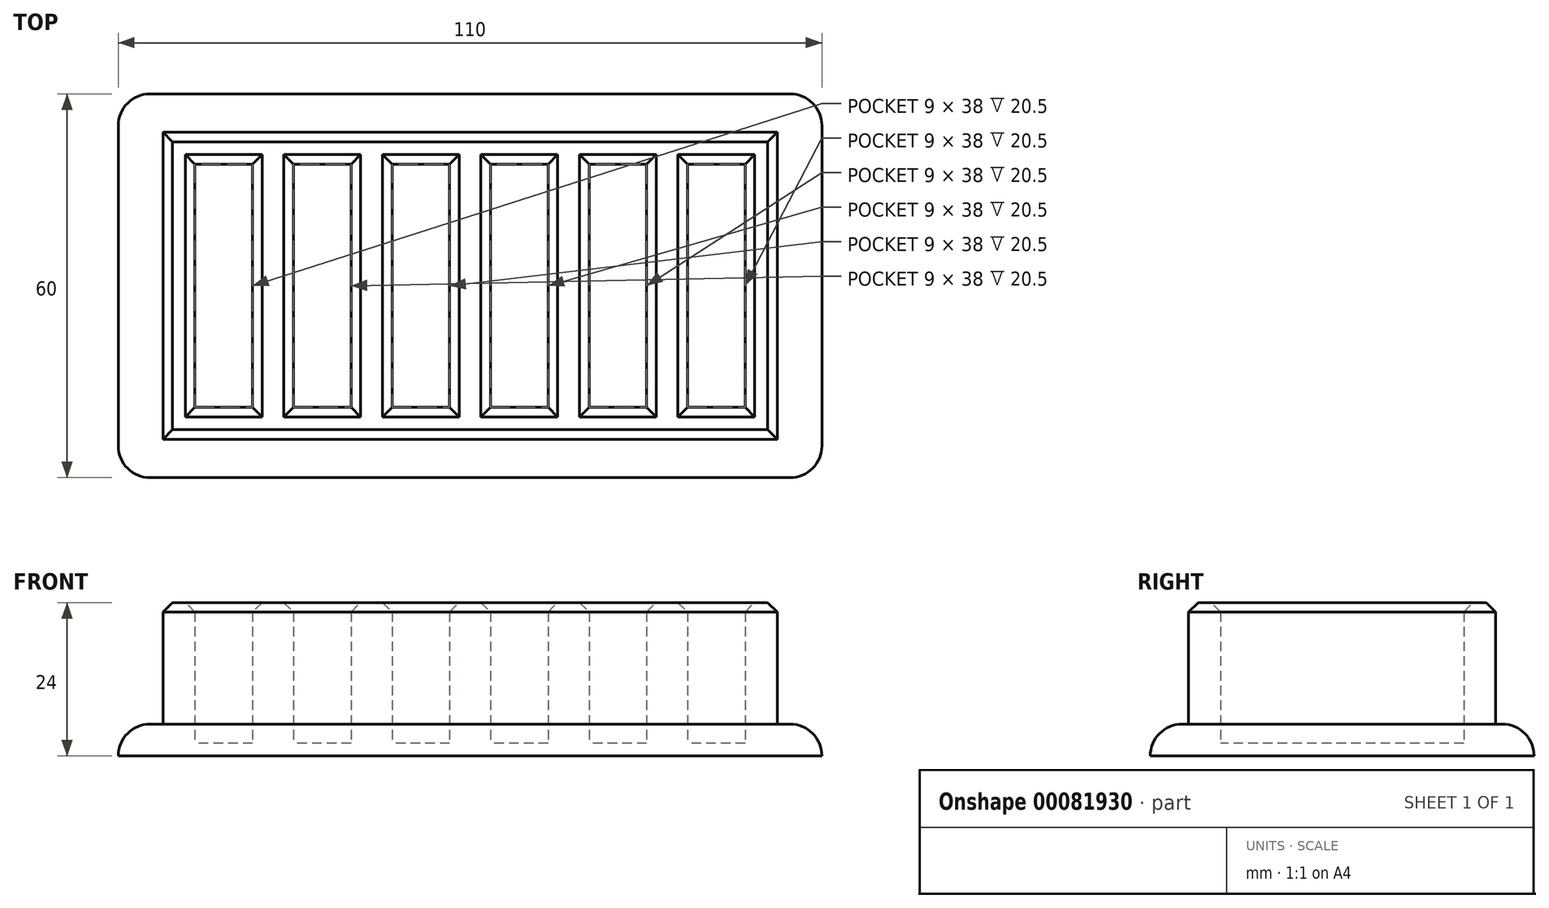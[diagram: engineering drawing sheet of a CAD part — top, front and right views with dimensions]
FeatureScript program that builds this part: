
annotation { "Feature Type Name" : "Feature", "Feature Type Description" : "" }
export const myFeature = defineFeature(function(context is Context, id is Id, definition is map)
    precondition{}
    {
        {
            var Q0;
            Q0=qCreatedBy(makeId("Top.planeOp"),FACE);
            var sketch = newSketch(context, id + "F0", { "sketchPlane" : qUnion([Q0])});
            skLineSegment(sketch, "E0.rect.bottom", {"start": v(48, 24) * mm, "end": v(-48, 24) * mm});
            skLineSegment(sketch, "E0.rect.top", {"start": v(48, -24) * mm, "end": v(-48, -24) * mm});
            skLineSegment(sketch, "E0.rect.left", {"start": v(48, 24) * mm, "end": v(48, -24) * mm});
            skLineSegment(sketch, "E0.rect.right", {"start": v(-48, 24) * mm, "end": v(-48, -24) * mm});
            skPoint(sketch, "E0.rect.middle", {"position": v(0, 0) * mm});
            skLineSegment(sketch, "E1.rect.bottom", {"start": v(-55, 30) * mm, "end": v(55, 30) * mm});
            skLineSegment(sketch, "E1.rect.top", {"start": v(-55, -30) * mm, "end": v(55, -30) * mm});
            skLineSegment(sketch, "E1.rect.left", {"start": v(-55, 30) * mm, "end": v(-55, -30) * mm});
            skLineSegment(sketch, "E1.rect.right", {"start": v(55, 30) * mm, "end": v(55, -30) * mm});
            skSolve(sketch);
        }
        {
            var Q0;
            Q0=makeQuery(id+"F0.imprint","IMPRINT",FACE,{"disambiguationData":[TD([[makeQuery(id+"F0.imprint","IMPRINT",EDGE,{"derivedFrom":sQuery(id+"F0.wireOp",EDGE,"E0.rect.bottom")}),1.0]])]});
            extrude(context, id + "F1", {"entities" : qUnion([Q0]), "depth" : 2 * mm});
        }
        {
            var Q0;
            Q0=makeQuery(id+"F1.opExtrude","CAP_FACE",FACE,{"disambiguationData":[OSD([sQuery(id+"F0.wireOp",EDGE,"E0.rect.bottom"),sQuery(id+"F0.wireOp",EDGE,"E0.rect.top"),sQuery(id+"F0.wireOp",EDGE,"E0.rect.left"),sQuery(id+"F0.wireOp",EDGE,"E0.rect.right")])],"isStart":false});
            var sketch = newSketch(context, id + "F2", { "sketchPlane" : qUnion([Q0])});
            skLineSegment(sketch, "E2.rect.bottom", {"start": v(-34, 19) * mm, "end": v(-43, 19) * mm});
            skLineSegment(sketch, "E2.rect.top", {"start": v(-34, -19) * mm, "end": v(-43, -19) * mm});
            skLineSegment(sketch, "E2.rect.left", {"start": v(-34, 19) * mm, "end": v(-34, -19) * mm});
            skLineSegment(sketch, "E2.rect.right", {"start": v(-43, 19) * mm, "end": v(-43, -19) * mm});
            skPoint(sketch, "E2.rect.middle", {"position": v(-38.5, 0) * mm});
            skLineSegment(sketch, "E3.1.0.0", {"start": v(-18.6, 19) * mm, "end": v(-18.6, -19) * mm});
            skLineSegment(sketch, "E3.1.0.1", {"start": v(-27.6, 19) * mm, "end": v(-27.6, -19) * mm});
            skLineSegment(sketch, "E3.1.0.2", {"start": v(-18.6, 19) * mm, "end": v(-27.6, 19) * mm});
            skLineSegment(sketch, "E3.1.0.3", {"start": v(-18.6, -19) * mm, "end": v(-27.6, -19) * mm});
            skLineSegment(sketch, "E3.2.0.0", {"start": v(-3.2, 19) * mm, "end": v(-3.2, -19) * mm});
            skLineSegment(sketch, "E3.2.0.1", {"start": v(-12.2, 19) * mm, "end": v(-12.2, -19) * mm});
            skLineSegment(sketch, "E3.2.0.2", {"start": v(-3.2, 19) * mm, "end": v(-12.2, 19) * mm});
            skLineSegment(sketch, "E3.2.0.3", {"start": v(-3.2, -19) * mm, "end": v(-12.2, -19) * mm});
            skLineSegment(sketch, "E3.3.0.0", {"start": v(12.2, 19) * mm, "end": v(12.2, -19) * mm});
            skLineSegment(sketch, "E3.3.0.1", {"start": v(3.2, 19) * mm, "end": v(3.2, -19) * mm});
            skLineSegment(sketch, "E3.3.0.2", {"start": v(12.2, 19) * mm, "end": v(3.2, 19) * mm});
            skLineSegment(sketch, "E3.3.0.3", {"start": v(12.2, -19) * mm, "end": v(3.2, -19) * mm});
            skLineSegment(sketch, "E3.4.0.0", {"start": v(27.6, 19) * mm, "end": v(27.6, -19) * mm});
            skLineSegment(sketch, "E3.4.0.1", {"start": v(18.6, 19) * mm, "end": v(18.6, -19) * mm});
            skLineSegment(sketch, "E3.4.0.2", {"start": v(27.6, 19) * mm, "end": v(18.6, 19) * mm});
            skLineSegment(sketch, "E3.4.0.3", {"start": v(27.6, -19) * mm, "end": v(18.6, -19) * mm});
            skLineSegment(sketch, "E3.5.0.0", {"start": v(43, 19) * mm, "end": v(43, -19) * mm});
            skLineSegment(sketch, "E3.5.0.1", {"start": v(34, 19) * mm, "end": v(34, -19) * mm});
            skLineSegment(sketch, "E3.5.0.2", {"start": v(43, 19) * mm, "end": v(34, 19) * mm});
            skLineSegment(sketch, "E3.5.0.3", {"start": v(43, -19) * mm, "end": v(34, -19) * mm});
            skLineSegment(sketch, "E3.direction1", {"start": v(-43, -19) * mm, "end": v(-27.6, -19) * mm, "construction": true});
            skSolve(sketch);
        }
        {
            var Q0;
            Q0=makeQuery(id+"F2.imprint","IMPRINT",FACE,{"disambiguationData":[TD([[makeQuery(id+"F2.imprint","IMPRINT",EDGE,{"derivedFrom":sQuery(id+"F2.wireOp",EDGE,"E2.rect.bottom")}),-1.0]])]});
            extrude(context, id + "F3", {"entities" : qUnion([Q0]), "operationType" : NewBodyOperationType.ADD, "depth" : 22 * mm});
        }
        {
            var Q0;
            Q0=makeQuery(id+"F0.imprint","IMPRINT",FACE,{"disambiguationData":[TD([[makeQuery(id+"F0.imprint","IMPRINT",EDGE,{"derivedFrom":sQuery(id+"F0.wireOp",EDGE,"E0.rect.bottom")}),-1.0]])]});
            extrude(context, id + "F4", {"entities" : qUnion([Q0]), "operationType" : NewBodyOperationType.ADD, "depth" : 5 * mm});
        }
        {
            var Q0;
            Q0=makeQuery(id+"F4.opExtrude","CAP_EDGE",EDGE,{"disambiguationData":[OSD([sQuery(id+"F0.wireOp",EDGE,"E1.rect.top")])],"isStart":false});
            var Q1;
            Q1=makeQuery(id+"F4.opExtrude","CAP_EDGE",EDGE,{"disambiguationData":[OSD([sQuery(id+"F0.wireOp",EDGE,"E1.rect.left")])],"isStart":false});
            var Q2;
            Q2=makeQuery(id+"F4.opExtrude","CAP_EDGE",EDGE,{"disambiguationData":[OSD([sQuery(id+"F0.wireOp",EDGE,"E1.rect.bottom")])],"isStart":false});
            var Q3;
            Q3=makeQuery(id+"F4.opExtrude","CAP_EDGE",EDGE,{"disambiguationData":[OSD([sQuery(id+"F0.wireOp",EDGE,"E1.rect.right")])],"isStart":false});
            var Q4;
            Q4=makeQuery(id+"F4.opExtrude","SWEPT_EDGE",EDGE,{"disambiguationData":[OSD([sQuery(id+"F0.wireOp",EDGE,"E1.rect.top"),sQuery(id+"F0.wireOp",EDGE,"E1.rect.right")])]});
            var Q5;
            Q5=makeQuery(id+"F4.opExtrude","SWEPT_EDGE",EDGE,{"disambiguationData":[OSD([sQuery(id+"F0.wireOp",EDGE,"E1.rect.bottom"),sQuery(id+"F0.wireOp",EDGE,"E1.rect.right")])]});
            var Q6;
            Q6=makeQuery(id+"F4.opExtrude","SWEPT_EDGE",EDGE,{"disambiguationData":[OSD([sQuery(id+"F0.wireOp",EDGE,"E1.rect.top"),sQuery(id+"F0.wireOp",EDGE,"E1.rect.left")])]});
            var Q7;
            Q7=makeQuery(id+"F4.opExtrude","SWEPT_EDGE",EDGE,{"disambiguationData":[OSD([sQuery(id+"F0.wireOp",EDGE,"E1.rect.bottom"),sQuery(id+"F0.wireOp",EDGE,"E1.rect.left")])]});
            fillet(context, id + "F5", {"entities" : qUnion([Q0, Q1, Q2, Q3, Q4, Q5, Q6, Q7]), "radius" : 5 * mm, "tangentPropagation" : true, "allowEdgeOverflow" : false});
        }
        {
            var Q0;
            Q0=makeQuery(id+"F3.opExtrude","CAP_EDGE",EDGE,{"disambiguationData":[OSD([sQuery(id+"F0.wireOp",EDGE,"E0.rect.top")])],"isStart":false});
            var Q1;
            Q1=makeQuery(id+"F3.opExtrude","CAP_EDGE",EDGE,{"disambiguationData":[OSD([sQuery(id+"F0.wireOp",EDGE,"E0.rect.right")])],"isStart":false});
            var Q2;
            Q2=makeQuery(id+"F3.opExtrude","CAP_EDGE",EDGE,{"disambiguationData":[OSD([sQuery(id+"F0.wireOp",EDGE,"E0.rect.bottom")])],"isStart":false});
            var Q3;
            Q3=makeQuery(id+"F3.opExtrude","CAP_EDGE",EDGE,{"disambiguationData":[OSD([sQuery(id+"F0.wireOp",EDGE,"E0.rect.left")])],"isStart":false});
            var Q4;
            Q4=makeQuery(id+"F3.opExtrude","CAP_EDGE",EDGE,{"disambiguationData":[OSD([sQuery(id+"F2.wireOp",EDGE,"E2.rect.right")])],"isStart":false});
            var Q5;
            Q5=makeQuery(id+"F3.opExtrude","CAP_EDGE",EDGE,{"disambiguationData":[OSD([sQuery(id+"F2.wireOp",EDGE,"E2.rect.left")])],"isStart":false});
            var Q6;
            Q6=makeQuery(id+"F3.opExtrude","CAP_EDGE",EDGE,{"disambiguationData":[OSD([sQuery(id+"F2.wireOp",EDGE,"E2.rect.top")])],"isStart":false});
            var Q7;
            Q7=makeQuery(id+"F3.opExtrude","CAP_EDGE",EDGE,{"disambiguationData":[OSD([sQuery(id+"F2.wireOp",EDGE,"E2.rect.bottom")])],"isStart":false});
            var Q8;
            Q8=makeQuery(id+"F3.opExtrude","CAP_EDGE",EDGE,{"disambiguationData":[OSD([sQuery(id+"F2.wireOp",EDGE,"E3.1.0.3")])],"isStart":false});
            var Q9;
            Q9=makeQuery(id+"F3.opExtrude","CAP_EDGE",EDGE,{"disambiguationData":[OSD([sQuery(id+"F2.wireOp",EDGE,"E3.1.0.0")])],"isStart":false});
            var Q10;
            Q10=makeQuery(id+"F3.opExtrude","CAP_EDGE",EDGE,{"disambiguationData":[OSD([sQuery(id+"F2.wireOp",EDGE,"E3.1.0.1")])],"isStart":false});
            var Q11;
            Q11=makeQuery(id+"F3.opExtrude","CAP_EDGE",EDGE,{"disambiguationData":[OSD([sQuery(id+"F2.wireOp",EDGE,"E3.1.0.2")])],"isStart":false});
            var Q12;
            Q12=makeQuery(id+"F3.opExtrude","CAP_EDGE",EDGE,{"disambiguationData":[OSD([sQuery(id+"F2.wireOp",EDGE,"E3.2.0.2")])],"isStart":false});
            var Q13;
            Q13=makeQuery(id+"F3.opExtrude","CAP_EDGE",EDGE,{"disambiguationData":[OSD([sQuery(id+"F2.wireOp",EDGE,"E3.2.0.1")])],"isStart":false});
            var Q14;
            Q14=makeQuery(id+"F3.opExtrude","CAP_EDGE",EDGE,{"disambiguationData":[OSD([sQuery(id+"F2.wireOp",EDGE,"E3.2.0.3")])],"isStart":false});
            var Q15;
            Q15=makeQuery(id+"F3.opExtrude","CAP_EDGE",EDGE,{"disambiguationData":[OSD([sQuery(id+"F2.wireOp",EDGE,"E3.2.0.0")])],"isStart":false});
            var Q16;
            Q16=makeQuery(id+"F3.opExtrude","CAP_EDGE",EDGE,{"disambiguationData":[OSD([sQuery(id+"F2.wireOp",EDGE,"E3.3.0.1")])],"isStart":false});
            var Q17;
            Q17=makeQuery(id+"F3.opExtrude","CAP_EDGE",EDGE,{"disambiguationData":[OSD([sQuery(id+"F2.wireOp",EDGE,"E3.3.0.0")])],"isStart":false});
            var Q18;
            Q18=makeQuery(id+"F3.opExtrude","CAP_EDGE",EDGE,{"disambiguationData":[OSD([sQuery(id+"F2.wireOp",EDGE,"E3.3.0.3")])],"isStart":false});
            var Q19;
            Q19=makeQuery(id+"F3.opExtrude","CAP_EDGE",EDGE,{"disambiguationData":[OSD([sQuery(id+"F2.wireOp",EDGE,"E3.3.0.2")])],"isStart":false});
            var Q20;
            Q20=makeQuery(id+"F3.opExtrude","CAP_EDGE",EDGE,{"disambiguationData":[OSD([sQuery(id+"F2.wireOp",EDGE,"E3.4.0.1")])],"isStart":false});
            var Q21;
            Q21=makeQuery(id+"F3.opExtrude","CAP_EDGE",EDGE,{"disambiguationData":[OSD([sQuery(id+"F2.wireOp",EDGE,"E3.4.0.2")])],"isStart":false});
            var Q22;
            Q22=makeQuery(id+"F3.opExtrude","CAP_EDGE",EDGE,{"disambiguationData":[OSD([sQuery(id+"F2.wireOp",EDGE,"E3.4.0.0")])],"isStart":false});
            var Q23;
            Q23=makeQuery(id+"F3.opExtrude","CAP_EDGE",EDGE,{"disambiguationData":[OSD([sQuery(id+"F2.wireOp",EDGE,"E3.4.0.3")])],"isStart":false});
            var Q24;
            Q24=makeQuery(id+"F3.opExtrude","CAP_EDGE",EDGE,{"disambiguationData":[OSD([sQuery(id+"F2.wireOp",EDGE,"E3.5.0.3")])],"isStart":false});
            var Q25;
            Q25=makeQuery(id+"F3.opExtrude","CAP_EDGE",EDGE,{"disambiguationData":[OSD([sQuery(id+"F2.wireOp",EDGE,"E3.5.0.1")])],"isStart":false});
            var Q26;
            Q26=makeQuery(id+"F3.opExtrude","CAP_EDGE",EDGE,{"disambiguationData":[OSD([sQuery(id+"F2.wireOp",EDGE,"E3.5.0.0")])],"isStart":false});
            var Q27;
            Q27=makeQuery(id+"F3.opExtrude","CAP_EDGE",EDGE,{"disambiguationData":[OSD([sQuery(id+"F2.wireOp",EDGE,"E3.5.0.2")])],"isStart":false});
            var Q28;
            Q28=makeQuery(id+"F3.opExtrude","CAP_EDGE",EDGE,{"disambiguationData":[OSD([sQuery(id+"F2.wireOp",EDGE,"E3.6.0.1")])],"isStart":false});
            var Q29;
            Q29=makeQuery(id+"F3.opExtrude","CAP_EDGE",EDGE,{"disambiguationData":[OSD([sQuery(id+"F2.wireOp",EDGE,"E3.6.0.2")])],"isStart":false});
            var Q30;
            Q30=makeQuery(id+"F3.opExtrude","CAP_EDGE",EDGE,{"disambiguationData":[OSD([sQuery(id+"F2.wireOp",EDGE,"E3.6.0.0")])],"isStart":false});
            var Q31;
            Q31=makeQuery(id+"F3.opExtrude","CAP_EDGE",EDGE,{"disambiguationData":[OSD([sQuery(id+"F2.wireOp",EDGE,"E3.6.0.3")])],"isStart":false});
            var Q32;
            Q32=makeQuery(id+"F3.opExtrude","CAP_EDGE",EDGE,{"disambiguationData":[OSD([sQuery(id+"F2.wireOp",EDGE,"E3.7.0.3")])],"isStart":false});
            var Q33;
            Q33=makeQuery(id+"F3.opExtrude","CAP_EDGE",EDGE,{"disambiguationData":[OSD([sQuery(id+"F2.wireOp",EDGE,"E3.7.0.1")])],"isStart":false});
            var Q34;
            Q34=makeQuery(id+"F3.opExtrude","CAP_EDGE",EDGE,{"disambiguationData":[OSD([sQuery(id+"F2.wireOp",EDGE,"E3.7.0.0")])],"isStart":false});
            var Q35;
            Q35=makeQuery(id+"F3.opExtrude","CAP_EDGE",EDGE,{"disambiguationData":[OSD([sQuery(id+"F2.wireOp",EDGE,"E3.7.0.2")])],"isStart":false});
            var Q36;
            Q36=makeQuery(id+"F3.opExtrude","CAP_EDGE",EDGE,{"disambiguationData":[OSD([sQuery(id+"F2.wireOp",EDGE,"E3.8.0.1")])],"isStart":false});
            var Q37;
            Q37=makeQuery(id+"F3.opExtrude","CAP_EDGE",EDGE,{"disambiguationData":[OSD([sQuery(id+"F2.wireOp",EDGE,"E3.8.0.3")])],"isStart":false});
            var Q38;
            Q38=makeQuery(id+"F3.opExtrude","CAP_EDGE",EDGE,{"disambiguationData":[OSD([sQuery(id+"F2.wireOp",EDGE,"E3.8.0.0")])],"isStart":false});
            var Q39;
            Q39=makeQuery(id+"F3.opExtrude","CAP_EDGE",EDGE,{"disambiguationData":[OSD([sQuery(id+"F2.wireOp",EDGE,"E3.8.0.2")])],"isStart":false});
            var Q40;
            Q40=makeQuery(id+"F3.opExtrude","CAP_EDGE",EDGE,{"disambiguationData":[OSD([sQuery(id+"F2.wireOp",EDGE,"E3.9.0.1")])],"isStart":false});
            var Q41;
            Q41=makeQuery(id+"F3.opExtrude","CAP_EDGE",EDGE,{"disambiguationData":[OSD([sQuery(id+"F2.wireOp",EDGE,"E3.9.0.3")])],"isStart":false});
            var Q42;
            Q42=makeQuery(id+"F3.opExtrude","CAP_EDGE",EDGE,{"disambiguationData":[OSD([sQuery(id+"F2.wireOp",EDGE,"E3.9.0.0")])],"isStart":false});
            var Q43;
            Q43=makeQuery(id+"F3.opExtrude","CAP_EDGE",EDGE,{"disambiguationData":[OSD([sQuery(id+"F2.wireOp",EDGE,"E3.9.0.2")])],"isStart":false});
            chamfer(context, id + "F6", {"entities" : qUnion([Q0, Q1, Q2, Q3, Q4, Q5, Q6, Q7, Q8, Q9, Q10, Q11, Q12, Q13, Q14, Q15, Q16, Q17, Q18, Q19, Q20, Q21, Q22, Q23, Q24, Q25, Q26, Q27, Q28, Q29, Q30, Q31, Q32, Q33, Q34, Q35, Q36, Q37, Q38, Q39, Q40, Q41, Q42, Q43]), "width" : 1.5 * mm, "tangentPropagation" : true});
        }
    });
